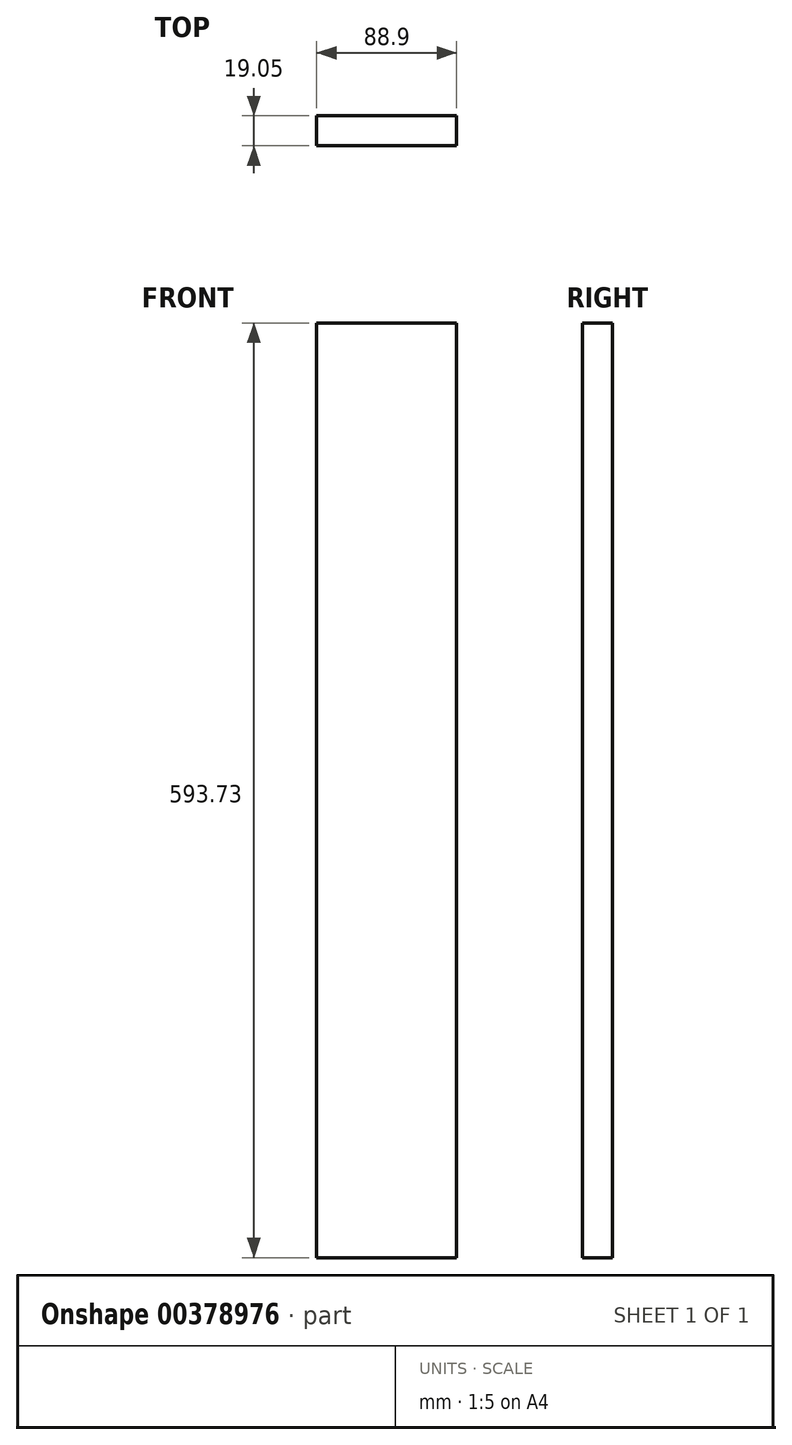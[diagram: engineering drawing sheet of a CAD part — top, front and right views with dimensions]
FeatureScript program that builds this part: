
annotation { "Feature Type Name" : "Feature", "Feature Type Description" : "" }
export const myFeature = defineFeature(function(context is Context, id is Id, definition is map)
    precondition{}
    {
        {
            var Q0;
            Q0=qCreatedBy(makeId("Front.planeOp"),FACE);
            var sketch = newSketch(context, id + "F0", { "sketchPlane" : qUnion([Q0])});
            skLineSegment(sketch, "E0.bottom", {"start": v(-88.9, 430.45) * mm, "end": v(0, 430.45) * mm});
            skLineSegment(sketch, "E0.top", {"start": v(-88.9, -163.28) * mm, "end": v(0, -163.28) * mm});
            skLineSegment(sketch, "E0.left", {"start": v(-88.9, 430.45) * mm, "end": v(-88.9, -163.28) * mm});
            skLineSegment(sketch, "E0.right", {"start": v(0, 430.45) * mm, "end": v(0, -163.28) * mm});
            skSolve(sketch);
        }
        {
            var Q0;
            Q0=makeQuery(id+"F0.imprint","IMPRINT",FACE,{"disambiguationData":[TD([[makeQuery(id+"F0.imprint","IMPRINT",EDGE,{"derivedFrom":sQuery(id+"F0.wireOp",EDGE,"E0.bottom")}),-1.0]])]});
            extrude(context, id + "F1", {"entities" : qUnion([Q0]), "depth" : 19.05 * mm, "offsetDistance" : 25.4 * mm});
        }
    });
